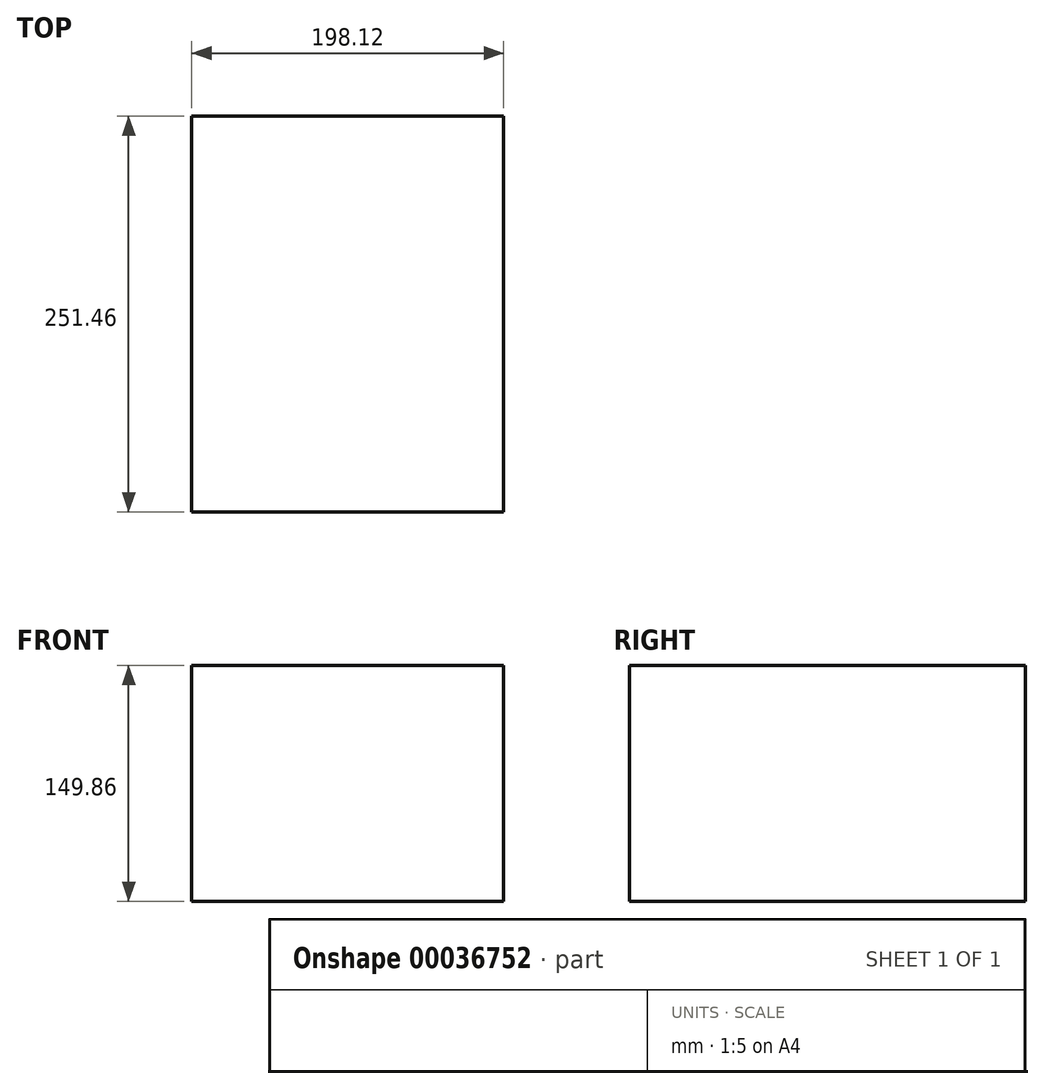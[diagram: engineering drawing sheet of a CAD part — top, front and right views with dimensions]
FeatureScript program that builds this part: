
annotation { "Feature Type Name" : "Feature", "Feature Type Description" : "" }
export const myFeature = defineFeature(function(context is Context, id is Id, definition is map)
    precondition{}
    {
        {
            var Q0;
            Q0=qCreatedBy(makeId("Front.planeOp"),FACE);
            var sketch = newSketch(context, id + "F0", { "sketchPlane" : qUnion([Q0])});
            skLineSegment(sketch, "E0", {"start": v(0, 74.93) * mm, "end": v(99.06, 74.93) * mm});
            skLineSegment(sketch, "E1", {"start": v(99.06, 74.93) * mm, "end": v(99.06, 0) * mm});
            skLineSegment(sketch, "E2.MirrorCS", {"start": v(0, 74.93) * mm, "end": v(-99.06, 74.93) * mm});
            skLineSegment(sketch, "E3.MirrorCS", {"start": v(-99.06, 74.93) * mm, "end": v(-99.06, 0) * mm});
            skLineSegment(sketch, "E4.MirrorCS", {"start": v(99.06, -74.93) * mm, "end": v(99.06, 0) * mm});
            skLineSegment(sketch, "E5.MirrorCS", {"start": v(0, -74.93) * mm, "end": v(99.06, -74.93) * mm});
            skLineSegment(sketch, "E6.MirrorCS", {"start": v(0, -74.93) * mm, "end": v(-99.06, -74.93) * mm});
            skLineSegment(sketch, "E7.MirrorCS", {"start": v(-99.06, -74.93) * mm, "end": v(-99.06, 0) * mm});
            skSolve(sketch);
        }
        {
            var Q0;
            Q0=makeQuery(id+"F0.imprint","IMPRINT",FACE,{"disambiguationData":[TD([[makeQuery(id+"F0.imprint","IMPRINT",EDGE,{"derivedFrom":sQuery(id+"F0.wireOp",EDGE,"E0")}),-1.0]])]});
            extrude(context, id + "F1", {"entities" : qUnion([Q0]), "endBound" : BoundingType.SYMMETRIC, "depth" : 251.46 * mm});
        }
    });
